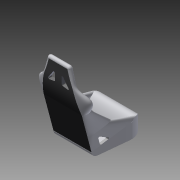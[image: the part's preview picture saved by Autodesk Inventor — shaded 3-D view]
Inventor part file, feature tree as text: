
AUTODESK INVENTOR PART (.ipt)
format: ipt  version: 2015 SP1 (Build 190203100, 203)  size: 1,276,416 bytes
history: native  units: in
note: dims shown in document units (in); Inventor stores cm internally (conversion verified against a paired STEP export)
features: other x2, imported_body x2, revolve x1
ambient origin geometry x8: Origin, YZ Plane, XZ Plane, XY Plane, X Axis, Y Axis, Z Axis, Center Point
bodies: Body1 (feature_tree), Body2 (feature_tree)
feature tree (5):
  revolve  "Revolve7"  [1 undecoded]
  other  "siege1"
  other  "Cut-Extrude11"
  imported_body  "Base1"
  imported_body  "Base2"
note: 1 required parameter value undecoded (feature->parameter linkage not recoverable at this tier; creation-order binding heuristic only, values carry confidence <= 0.55)
